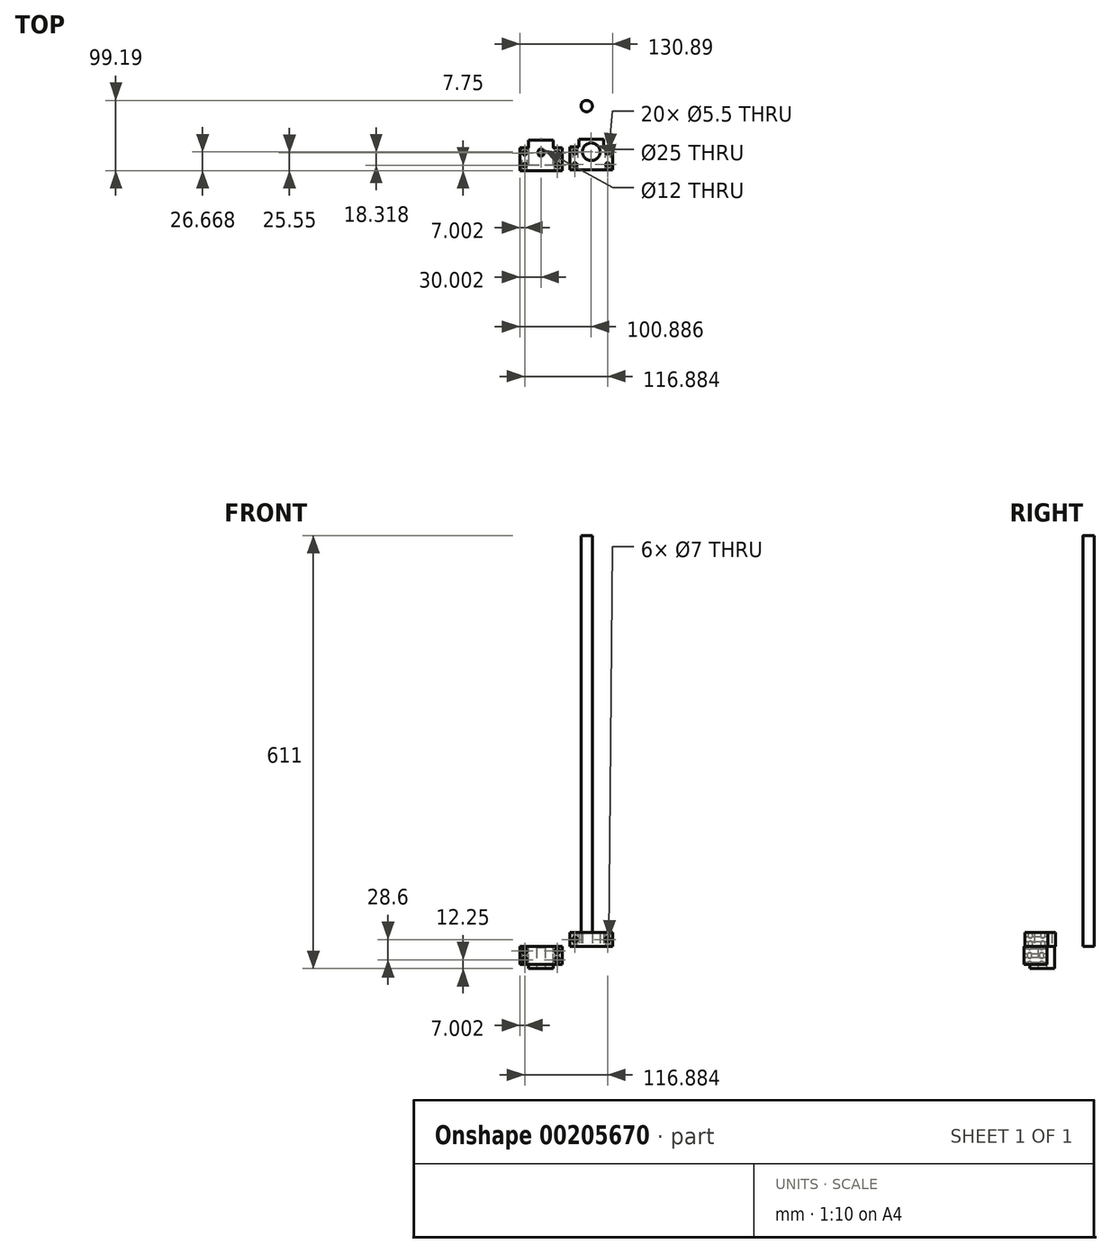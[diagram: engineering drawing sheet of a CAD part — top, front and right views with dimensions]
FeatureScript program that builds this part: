
annotation { "Feature Type Name" : "Feature", "Feature Type Description" : "" }
export const myFeature = defineFeature(function(context is Context, id is Id, definition is map)
    precondition{}
    {
        {
            var Q0;
            Q0=qCreatedBy(makeId("Top.planeOp"),FACE);
            var sketch = newSketch(context, id + "F0", { "sketchPlane" : qUnion([Q0])});
            skLineSegment(sketch, "E0.bottom", {"start": v(-59.54, -37.82) * mm, "end": v(0.46, -37.82) * mm});
            skLineSegment(sketch, "E0.top", {"start": v(-59.54, -5.32) * mm, "end": v(-47.09, -5.32) * mm});
            skLineSegment(sketch, "E0.left", {"start": v(-59.54, -37.82) * mm, "end": v(-59.54, -5.32) * mm});
            skLineSegment(sketch, "E0.right", {"start": v(0.46, -37.82) * mm, "end": v(0.46, -5.32) * mm});
            skLineSegment(sketch, "E1.top", {"start": v(-47.09, 5.28) * mm, "end": v(-11.99, 5.28) * mm});
            skLineSegment(sketch, "E1.left", {"start": v(-47.09, -5.32) * mm, "end": v(-47.09, 5.28) * mm});
            skLineSegment(sketch, "E1.right", {"start": v(-11.99, -5.32) * mm, "end": v(-11.99, 5.28) * mm});
            skLineSegment(sketch, "E2.trimOffspring", {"start": v(-11.99, -5.32) * mm, "end": v(0.46, -5.32) * mm});
            skLineSegment(sketch, "E3", {"start": v(-59.54, -5.32) * mm, "end": v(0.46, -37.82) * mm, "construction": true});
            skLineSegment(sketch, "E4.bottom", {"start": v(-52.54, -30.07) * mm, "end": v(-6.54, -30.07) * mm, "construction": true});
            skLineSegment(sketch, "E4.top", {"start": v(-52.54, -13.07) * mm, "end": v(-6.54, -13.07) * mm, "construction": true});
            skLineSegment(sketch, "E4.left", {"start": v(-52.54, -30.07) * mm, "end": v(-52.54, -13.07) * mm, "construction": true});
            skLineSegment(sketch, "E4.right", {"start": v(-6.54, -30.07) * mm, "end": v(-6.54, -13.07) * mm, "construction": true});
            skPoint(sketch, "E4.middle", {"position": v(-29.54, -21.57) * mm});
            skSolve(sketch);
        }
        {
            var Q0;
            Q0=makeQuery(id+"F0.imprint","IMPRINT",FACE,{"disambiguationData":[TD([[makeQuery(id+"F0.imprint","IMPRINT",EDGE,{"derivedFrom":sQuery(id+"F0.wireOp",EDGE,"E0.bottom")}),1.0]])]});
            extrude(context, id + "F1", {"entities" : qUnion([Q0]), "oppositeDirection" : true, "depth" : 25 * mm});
        }
        {
            var Q0;
            Q0=sQuery(id+"F0.wireOp",VERTEX,"E4.left.end");
            var Q1;
            Q1=sQuery(id+"F0.wireOp",VERTEX,"E4.bottom.start");
            var Q2;
            Q2=sQuery(id+"F0.wireOp",VERTEX,"E4.right.end");
            var Q3;
            Q3=sQuery(id+"F0.wireOp",VERTEX,"E4.right.start");
            var Q4;
            Q4=makeQuery(id+"F1.opExtrude","SWEPT_BODY",BODY,{"disambiguationData":[OSD([sQuery(id+"F0.wireOp",EDGE,"E0.bottom"),sQuery(id+"F0.wireOp",EDGE,"E0.top"),sQuery(id+"F0.wireOp",EDGE,"E0.left"),sQuery(id+"F0.wireOp",EDGE,"E0.right"),sQuery(id+"F0.wireOp",EDGE,"E1.top"),sQuery(id+"F0.wireOp",EDGE,"E1.left"),sQuery(id+"F0.wireOp",EDGE,"E1.right"),sQuery(id+"F0.wireOp",EDGE,"E2.trimOffspring")])]});
            hole(context, id + "F2", {"style" : HoleStyle.SIMPLE, "endStyle" : HoleEndStyle.BLIND, "standardTappedOrClearance" : lookupTablePath({ "standard" : "ISO", "fit" : "Normal", "size" : "M5", "type" : "Clearance" }), "standardBlindInLast" : lookupTablePath({ "fit" : "Standard", "standard" : "ISO", "size" : "M5", "type" : "Clearance" }), "holeDiameter" : 5.5 * mm, "holeDepth" : 25 * mm, "locations" : qUnion([Q0, Q1, Q2, Q3]), "scope" : qUnion([Q4])});
        }
        {
            var Q0;
            Q0=makeQuery(id+"F1.opExtrude","CAP_FACE",FACE,{"disambiguationData":[OSD([sQuery(id+"F0.wireOp",EDGE,"E0.bottom"),sQuery(id+"F0.wireOp",EDGE,"E0.top"),sQuery(id+"F0.wireOp",EDGE,"E0.left"),sQuery(id+"F0.wireOp",EDGE,"E0.right"),sQuery(id+"F0.wireOp",EDGE,"E1.top"),sQuery(id+"F0.wireOp",EDGE,"E1.left"),sQuery(id+"F0.wireOp",EDGE,"E1.right"),sQuery(id+"F0.wireOp",EDGE,"E2.trimOffspring")])],"isStart":false});
            var sketch = newSketch(context, id + "F3", { "sketchPlane" : qUnion([Q0])});
            skLineSegment(sketch, "E5", {"start": v(-47.09, -5.28) * mm, "end": v(-47.09, 29.82) * mm});
            skLineSegment(sketch, "E6", {"start": v(-47.09, 29.82) * mm, "end": v(-11.99, 29.82) * mm});
            skLineSegment(sketch, "E7", {"start": v(-11.99, 29.82) * mm, "end": v(-11.99, -5.28) * mm});
            skSolve(sketch);
        }
        {
            var Q0;
            {var subQ2=sQuery(id+"F3.wireOp",EDGE,"E6");Q0=makeQuery(id+"F3.imprint","IMPRINT",FACE,{"disambiguationData":[TD([[makeQuery(id+"F3.imprint","IMPRINT",EDGE,{"derivedFrom":subQ2}),-1.0]])]});}
            extrude(context, id + "F4", {"entities" : qUnion([Q0]), "operationType" : NewBodyOperationType.ADD, "depth" : 6 * mm});
        }
        {
            var Q0;
            Q0=makeQuery(id+"F4.opExtrude","CAP_FACE",FACE,{"disambiguationData":[OSD([sQuery(id+"F0.wireOp",EDGE,"E1.top"),sQuery(id+"F3.wireOp",EDGE,"E5"),sQuery(id+"F3.wireOp",EDGE,"E6"),sQuery(id+"F3.wireOp",EDGE,"E7")])],"isStart":false});
            var sketch = newSketch(context, id + "F5", { "sketchPlane" : qUnion([Q0])});
            skLineSegment(sketch, "E8", {"start": v(-11.99, -5.28) * mm, "end": v(-47.09, 29.82) * mm, "construction": true});
            skPoint(sketch, "E9", {"position": v(-29.54, 12.27) * mm});
            skSolve(sketch);
        }
        {
            var Q0;
            Q0=sQuery(id+"F5.wireOp",VERTEX,"E9");
            var Q1;
            Q1=makeQuery(id+"F1.opExtrude","SWEPT_BODY",BODY,{"disambiguationData":[OSD([sQuery(id+"F0.wireOp",EDGE,"E0.bottom"),sQuery(id+"F0.wireOp",EDGE,"E0.top"),sQuery(id+"F0.wireOp",EDGE,"E0.left"),sQuery(id+"F0.wireOp",EDGE,"E0.right"),sQuery(id+"F0.wireOp",EDGE,"E1.top"),sQuery(id+"F0.wireOp",EDGE,"E1.left"),sQuery(id+"F0.wireOp",EDGE,"E1.right"),sQuery(id+"F0.wireOp",EDGE,"E2.trimOffspring")])]});
            hole(context, id + "F6", {"style" : HoleStyle.SIMPLE, "endStyle" : HoleEndStyle.BLIND, "holeDiameter" : 12 * mm, "holeDepth" : 30 * mm, "locations" : qUnion([Q0]), "scope" : qUnion([Q1])});
        }
        {
            var Q0;
            Q0=makeQuery(id+"F1.opExtrude","SWEPT_FACE",FACE,{"disambiguationData":[OSD([sQuery(id+"F0.wireOp",EDGE,"E0.top")])]});
            var sketch = newSketch(context, id + "F7", { "sketchPlane" : qUnion([Q0])});
            skPoint(sketch, "E10.0", {"position": v(59.54, 0) * mm});
            skPoint(sketch, "E11.0", {"position": v(-0.46, -25) * mm});
            skLineSegment(sketch, "E12", {"start": v(-0.46, -25) * mm, "end": v(59.54, 0) * mm, "construction": true});
            skPoint(sketch, "E13", {"position": v(29.54, -12.5) * mm});
            skLineSegment(sketch, "E14.bottom", {"start": v(52.54, -18.75) * mm, "end": v(6.54, -18.75) * mm, "construction": true});
            skLineSegment(sketch, "E14.top", {"start": v(52.54, -6.25) * mm, "end": v(6.54, -6.25) * mm, "construction": true});
            skLineSegment(sketch, "E14.left", {"start": v(52.54, -18.75) * mm, "end": v(52.54, -6.25) * mm, "construction": true});
            skLineSegment(sketch, "E14.right", {"start": v(6.54, -18.75) * mm, "end": v(6.54, -6.25) * mm, "construction": true});
            skSolve(sketch);
        }
        {
            var Q0;
            Q0=sQuery(id+"F7.wireOp",VERTEX,"E14.bottom.end");
            var Q1;
            Q1=sQuery(id+"F7.wireOp",VERTEX,"E14.top.end");
            var Q2;
            Q2=sQuery(id+"F7.wireOp",VERTEX,"E14.left.end");
            var Q3;
            Q3=sQuery(id+"F7.wireOp",VERTEX,"E14.left.start");
            var Q4;
            Q4=makeQuery(id+"F1.opExtrude","SWEPT_BODY",BODY,{"disambiguationData":[OSD([sQuery(id+"F0.wireOp",EDGE,"E0.bottom"),sQuery(id+"F0.wireOp",EDGE,"E0.top"),sQuery(id+"F0.wireOp",EDGE,"E0.left"),sQuery(id+"F0.wireOp",EDGE,"E0.right"),sQuery(id+"F0.wireOp",EDGE,"E1.top"),sQuery(id+"F0.wireOp",EDGE,"E1.left"),sQuery(id+"F0.wireOp",EDGE,"E1.right"),sQuery(id+"F0.wireOp",EDGE,"E2.trimOffspring")])]});
            hole(context, id + "F8", {"style" : HoleStyle.SIMPLE, "endStyle" : HoleEndStyle.BLIND, "holeDiameter" : 7 * mm, "holeDepth" : 40 * mm, "locations" : qUnion([Q0, Q1, Q2, Q3]), "scope" : qUnion([Q4])});
        }
        {
            var Q0;
            Q0=qCreatedBy(makeId("Top.planeOp"),FACE);
            var sketch = newSketch(context, id + "F9", { "sketchPlane" : qUnion([Q0])});
            skLineSegment(sketch, "E15.bottom", {"start": v(71.35, -36.75) * mm, "end": v(11.35, -36.75) * mm});
            skLineSegment(sketch, "E15.top", {"start": v(71.35, -4.25) * mm, "end": v(58.85, -4.25) * mm});
            skLineSegment(sketch, "E15.left", {"start": v(71.35, -36.75) * mm, "end": v(71.35, -4.25) * mm});
            skLineSegment(sketch, "E15.right", {"start": v(11.35, -36.75) * mm, "end": v(11.35, -4.25) * mm});
            skPoint(sketch, "E15.middle", {"position": v(41.35, -20.5) * mm});
            skLineSegment(sketch, "E16.top", {"start": v(58.85, 6.35) * mm, "end": v(23.85, 6.35) * mm});
            skLineSegment(sketch, "E16.left", {"start": v(58.85, -4.25) * mm, "end": v(58.85, 6.35) * mm});
            skLineSegment(sketch, "E16.right", {"start": v(23.85, -4.25) * mm, "end": v(23.85, 6.35) * mm});
            skPoint(sketch, "E16.middle", {"position": v(41.35, -4.25) * mm});
            skLineSegment(sketch, "E17.trimOffspring", {"start": v(23.85, -4.25) * mm, "end": v(11.35, -4.25) * mm});
            skPoint(sketch, "E16.bottom.end.orphan", {"position": v(23.85, -14.85) * mm});
            skPoint(sketch, "E18.orphan", {"position": v(58.85, -14.85) * mm});
            skLineSegment(sketch, "E19", {"start": v(23.85, -4.25) * mm, "end": v(23.85, -28.65) * mm, "construction": true});
            skLineSegment(sketch, "E20", {"start": v(23.85, -28.65) * mm, "end": v(58.85, -28.65) * mm, "construction": true});
            skLineSegment(sketch, "E21", {"start": v(58.85, -28.65) * mm, "end": v(58.85, -4.25) * mm, "construction": true});
            skLineSegment(sketch, "E22", {"start": v(58.85, 6.35) * mm, "end": v(23.85, -28.65) * mm, "construction": true});
            skPoint(sketch, "E23", {"position": v(41.35, -11.15) * mm});
            skCircle(sketch, "E24", {"center": v(41.35, -11.15) * mm, "radius": 12.5 * mm});
            skLineSegment(sketch, "E25", {"start": v(11.35, -4.25) * mm, "end": v(71.35, -36.75) * mm, "construction": true});
            skLineSegment(sketch, "E26.bottom", {"start": v(18.35, -29.25) * mm, "end": v(64.35, -29.25) * mm, "construction": true});
            skLineSegment(sketch, "E26.top", {"start": v(18.35, -11.75) * mm, "end": v(64.35, -11.75) * mm, "construction": true});
            skLineSegment(sketch, "E26.left", {"start": v(18.35, -29.25) * mm, "end": v(18.35, -11.75) * mm, "construction": true});
            skLineSegment(sketch, "E26.right", {"start": v(64.35, -29.25) * mm, "end": v(64.35, -11.75) * mm, "construction": true});
            skSolve(sketch);
        }
        {
            var Q0;
            Q0=makeQuery(id+"F9.imprint","IMPRINT",FACE,{"disambiguationData":[TD([[makeQuery(id+"F9.imprint","IMPRINT",EDGE,{"derivedFrom":sQuery(id+"F9.wireOp",EDGE,"E15.bottom")}),-1.0]])]});
            extrude(context, id + "F10", {"entities" : qUnion([Q0]), "depth" : 19.7 * mm});
        }
        {
            var Q0;
            Q0=sQuery(id+"F9.wireOp",VERTEX,"E26.bottom.start");
            var Q1;
            Q1=sQuery(id+"F9.wireOp",VERTEX,"E26.left.end");
            var Q2;
            Q2=sQuery(id+"F9.wireOp",VERTEX,"E26.bottom.end");
            var Q3;
            Q3=sQuery(id+"F9.wireOp",VERTEX,"E26.top.end");
            var Q4;
            Q4=makeQuery(id+"F10.opExtrude","SWEPT_BODY",BODY,{"disambiguationData":[OSD([sQuery(id+"F9.wireOp",EDGE,"E15.bottom"),sQuery(id+"F9.wireOp",EDGE,"E15.top"),sQuery(id+"F9.wireOp",EDGE,"E15.left"),sQuery(id+"F9.wireOp",EDGE,"E15.right"),sQuery(id+"F9.wireOp",EDGE,"E16.top"),sQuery(id+"F9.wireOp",EDGE,"E16.left"),sQuery(id+"F9.wireOp",EDGE,"E16.right"),sQuery(id+"F9.wireOp",EDGE,"E17.trimOffspring"),sQuery(id+"F9.wireOp",EDGE,"E24")])]});
            hole(context, id + "F11", {"style" : HoleStyle.SIMPLE, "endStyle" : HoleEndStyle.BLIND, "oppositeDirection" : true, "holeDiameter" : 5.5 * mm, "holeDepth" : 40 * mm, "locations" : qUnion([Q0, Q1, Q2, Q3]), "scope" : qUnion([Q4])});
        }
        {
            var Q0;
            Q0=makeQuery(id+"F10.opExtrude","SWEPT_FACE",FACE,{"disambiguationData":[OSD([sQuery(id+"F9.wireOp",EDGE,"E15.bottom")])]});
            var sketch = newSketch(context, id + "F12", { "sketchPlane" : qUnion([Q0])});
            skLineSegment(sketch, "E27", {"start": v(11.35, 19.7) * mm, "end": v(71.35, 0) * mm, "construction": true});
            skLineSegment(sketch, "E28", {"start": v(71.35, 0) * mm, "end": v(41.35, 9.85) * mm, "construction": true});
            skLineSegment(sketch, "E29", {"start": v(41.35, 9.85) * mm, "end": v(64.35, 9.85) * mm, "construction": true});
            skLineSegment(sketch, "E30", {"start": v(41.35, 9.85) * mm, "end": v(18.35, 9.85) * mm, "construction": true});
            skSolve(sketch);
        }
        {
            var Q0;
            Q0=sQuery(id+"F12.wireOp",VERTEX,"E30.end");
            var Q1;
            Q1=sQuery(id+"F12.wireOp",VERTEX,"E29.end");
            var Q2;
            Q2=makeQuery(id+"F10.opExtrude","SWEPT_BODY",BODY,{"disambiguationData":[OSD([sQuery(id+"F9.wireOp",EDGE,"E15.bottom"),sQuery(id+"F9.wireOp",EDGE,"E15.top"),sQuery(id+"F9.wireOp",EDGE,"E15.left"),sQuery(id+"F9.wireOp",EDGE,"E15.right"),sQuery(id+"F9.wireOp",EDGE,"E16.top"),sQuery(id+"F9.wireOp",EDGE,"E16.left"),sQuery(id+"F9.wireOp",EDGE,"E16.right"),sQuery(id+"F9.wireOp",EDGE,"E17.trimOffspring"),sQuery(id+"F9.wireOp",EDGE,"E24")])]});
            hole(context, id + "F13", {"style" : HoleStyle.SIMPLE, "endStyle" : HoleEndStyle.BLIND, "holeDiameter" : 7 * mm, "holeDepth" : 40 * mm, "locations" : qUnion([Q0, Q1]), "scope" : qUnion([Q2])});
        }
        {
            var Q0;
            Q0=qCreatedBy(makeId("Top.planeOp"),FACE);
            var sketch = newSketch(context, id + "F14", { "sketchPlane" : qUnion([Q0])});
            skCircle(sketch, "E31", {"center": v(34.88, 53.37) * mm, "radius": 8 * mm});
            skSolve(sketch);
        }
        {
            var Q0;
            Q0=makeQuery(id+"F14.imprint","IMPRINT",FACE,{"disambiguationData":[TD([[makeQuery(id+"F14.imprint","IMPRINT",EDGE,{"derivedFrom":sQuery(id+"F14.wireOp",EDGE,"E31")}),1.0]])]});
            extrude(context, id + "F15", {"entities" : qUnion([Q0]), "depth" : 580 * mm});
        }
    });
